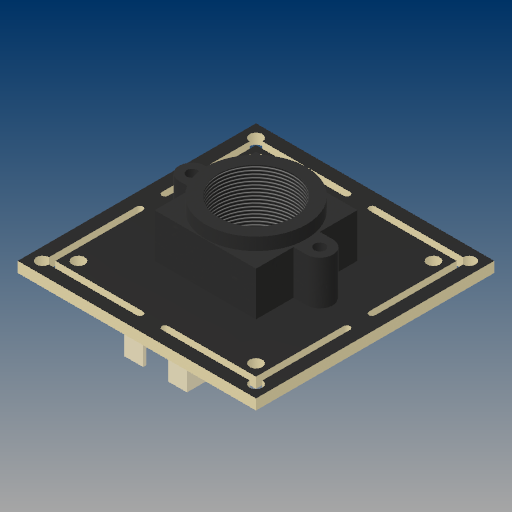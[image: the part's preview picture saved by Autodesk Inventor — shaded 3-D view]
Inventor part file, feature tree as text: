
AUTODESK INVENTOR PART (.ipt)
format: ipt  version: 2019 (Build 230136000, 136)  size: 297,472 bytes
history: native  units: mm
features: extrude x6, sketch x6, projected_geometry x2, fillet x1, thread x1
ambient origin geometry x8: Origin, YZ Plane, XZ Plane, XY Plane, X Axis, Y Axis, Z Axis, Center Point
bodies: Solid1 (feature_tree), Solid2 (feature_tree), Solid3 (feature_tree)
feature tree (16):
  extrude  "Extrusion1"  Depth=38.0mm
  fillet  "Fillet1"  Radius=2.0mm
  extrude  "Extrusion2"  Depth=2.0mm
  extrude  "Extrusion3"  Depth=2.0mm
  extrude  "Extrusion4"  Depth=2.0mm
  extrude  "Extrusion5"  Depth=2.0mm
  extrude  "Extrusion6"  Depth=3.0mm
  thread  "Thread1"  [1 undecoded]
  sketch  "Sketch1"  dims[d0=38.0mm d1=38.0mm d2=2.0mm]
  sketch  "Sketch2"  dims[d3=1.0mm d4=2.0mm]
  sketch  "Sketch3"  dims[d5=2.0mm d6=2.0mm]
  sketch  "Sketch4"  dims[d7=2.0mm d8=1.85mm]
  projected_geometry  "Projected Loop1"
  sketch  "Sketch5"  dims[d9=1.85mm d10=2.0mm]
  sketch  "Sketch6"  dims[d11=40.0mm d13=360.0deg d15=3.0mm d16=40.0mm d18=360.0deg d20=1.65mm d21=0.0mm d22=0.5mm d23=16.15mm d24=16.15mm d25=2.1mm d26=2.1mm d27=4.2mm d28=4.2mm d29=4.2mm d30=4.2mm d31=2.1mm d32=7.0mm d33=0.0mm d34=1.75mm d35=1.75mm d36=10.0mm d37=4.7mm d38=5.0mm d39=6.0mm d40=0.0mm d41=0.5mm d42=4.0mm d43=2.0mm d44=4.5mm d45=0.0mm d46=16.0mm d47=2.0mm d48=0.0mm d49=2.0mm d50=9.0mm d51=0.0mm d52=10.0mm d53=0.0mm]
  projected_geometry  "Projected Loop2"
note: 1 required parameter value undecoded (feature->parameter linkage not recoverable at this tier; creation-order binding heuristic only, values carry confidence <= 0.55)
